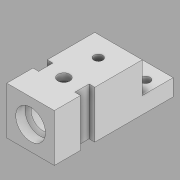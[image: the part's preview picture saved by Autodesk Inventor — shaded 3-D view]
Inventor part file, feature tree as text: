
AUTODESK INVENTOR PART (.ipt)
format: ipt  version: 2020 (Build 240168000, 168)  size: 198,656 bytes
history: native  units: in
note: dims shown in document units (in); Inventor stores cm internally (conversion verified against a paired STEP export)
features: sketch x8, extrude x6, other x1, hole x1, chamfer x1
ambient origin geometry x8: Origin, YZ Plane, XZ Plane, XY Plane, X Axis, Y Axis, Z Axis, Center Point
bodies: Body1 (feature_tree)
feature tree (17):
  other  "Sólido1"
  extrude  "BaseAlta"  Depth=3.7in
  extrude  "BaseBaja"  Depth=0.6in
  extrude  "Hexagono"  Depth=0.6in
  extrude  "DosAgujeros"  Depth=2.0in TaperAngle=0.0deg
  extrude  "AgujeroInferior"  Depth=1.3in
  extrude  "HoyoSuperior"  Depth=1.5in
  hole  "Agujero3"  [1 undecoded]
  chamfer  "Chaflán1"  Distance=1.7in
  sketch  "Boceto1"  dims[d0=2.0in d1=3.7in]
  sketch  "Boceto2"  dims[d2=1.1in d3=0.6in]
  sketch  "Boceto4"  dims[d4=0.24in d5=1.1in d6=0.6in]
  sketch  "Boceto6"  dims[d7=0.24in d8=2.0in d9=0.0in]
  sketch  "Boceto7"  dims[d10=2.0in d11=1.3in]
  sketch  "Boceto8"  dims[d12=0.7in d13=0.0in d19=1.5in]
  sketch  "Boceto9"  dims[d20=1.0in d21=1.0in d22=1.7in d23=0.0in]
  sketch  "Boceto10"  dims[d35=0.38in d36=0.38in d37=0.66in d38=0.66in d39=0.5in d40=0.5in d41=1.0in d42=0.4in d43=0.0in d44=0.6in d45=0.6in d46=0.5in d47=0.66in d48=0.5in d49=0.66in d50=0.3in d51=0.0in d52=1.0in d53=1.0in d54=1.0in d55=0.75in d56=1.25in d57=0.52in d58=0.5635in d59=2.0in d60=0.8108in d61=0.375in d62=1.0in d63=0.85in d64=0.5in d65=0.0in d66=1.0in d67=1.4in d68=0.31in d69=0.75in d70=0.5in d71=0.3in d72=0.5635in d73=0.5in d74=0.0in d76=0.125in d77=0.125in d78=45.0deg]
note: 1 required parameter value undecoded (feature->parameter linkage not recoverable at this tier; creation-order binding heuristic only, values carry confidence <= 0.55)
